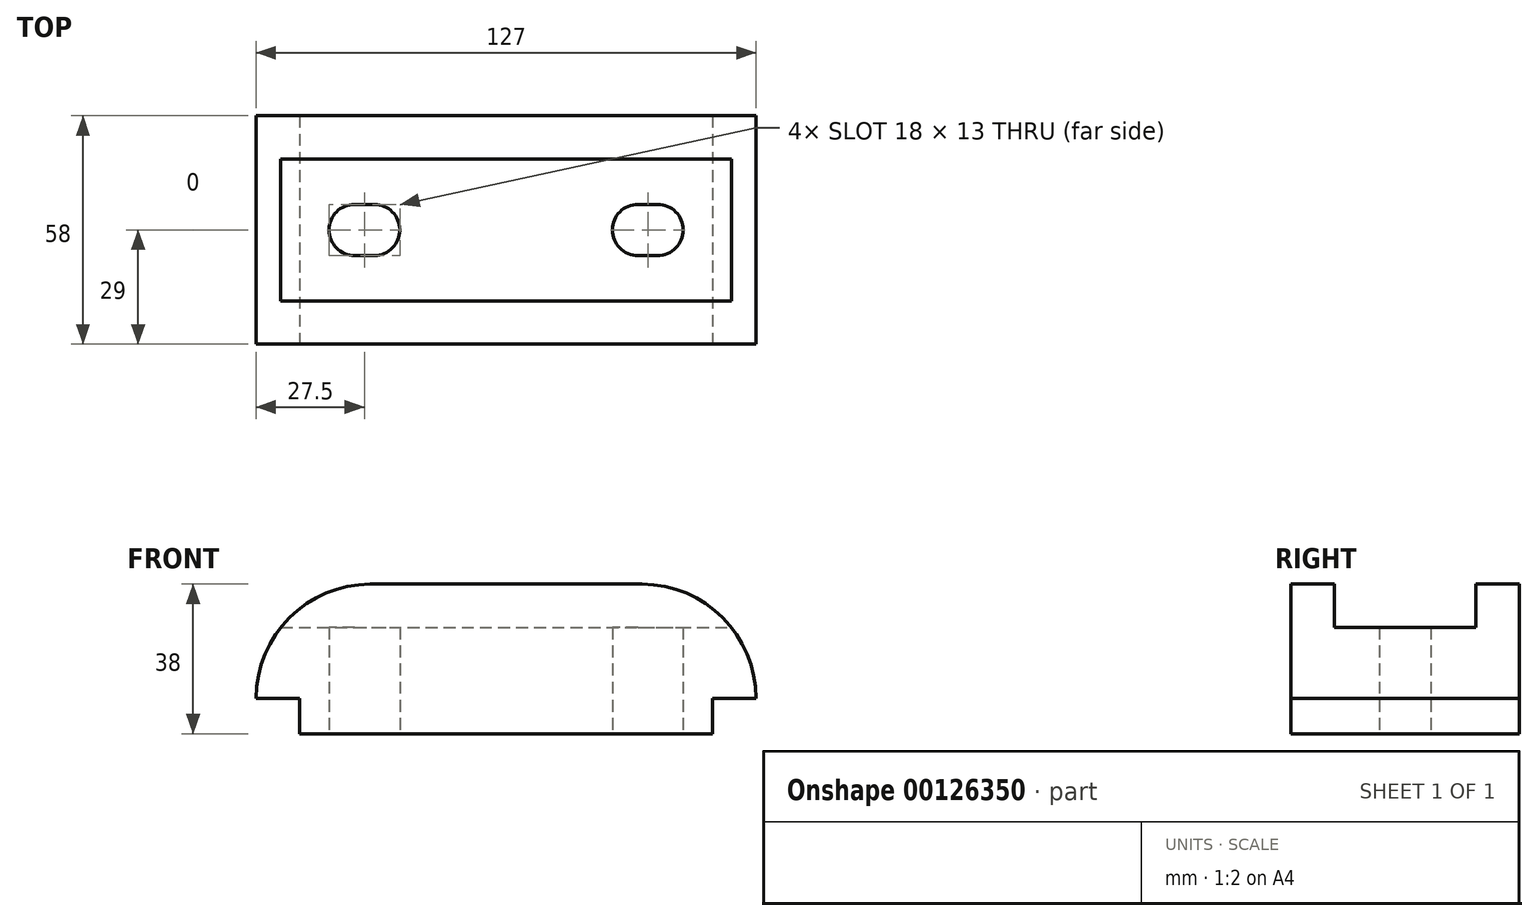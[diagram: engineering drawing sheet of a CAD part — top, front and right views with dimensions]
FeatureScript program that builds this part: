
annotation { "Feature Type Name" : "Feature", "Feature Type Description" : "" }
export const myFeature = defineFeature(function(context is Context, id is Id, definition is map)
    precondition{}
    {
        {
            var Q0;
            Q0=qCreatedBy(makeId("Front.planeOp"),FACE);
            var sketch = newSketch(context, id + "F0", { "sketchPlane" : qUnion([Q0])});
            skLineSegment(sketch, "E0", {"start": v(-63.5, 0) * mm, "end": v(63.5, 0) * mm});
            skLineSegment(sketch, "E1", {"start": v(52.5, 0) * mm, "end": v(52.5, 9) * mm});
            skLineSegment(sketch, "E2", {"start": v(52.5, 9) * mm, "end": v(63.5, 9) * mm});
            skLineSegment(sketch, "E3", {"start": v(-52.5, 0) * mm, "end": v(-52.5, 9) * mm});
            skLineSegment(sketch, "E4", {"start": v(-52.5, 9) * mm, "end": v(-63.5, 9) * mm});
            skLineSegment(sketch, "E5", {"start": v(63.5, 0) * mm, "end": v(63.5, 9) * mm, "construction": true});
            skLineSegment(sketch, "E6", {"start": v(-63.5, 0) * mm, "end": v(-63.5, 9) * mm, "construction": true});
            skPoint(sketch, "E7", {"position": v(0, 38) * mm});
            skLineSegment(sketch, "E8", {"start": v(-34.5, 38) * mm, "end": v(34.5, 38) * mm});
            skLineSegment(sketch, "E9", {"start": v(63.5, 9) * mm, "end": v(63.5, 9) * mm});
            skLineSegment(sketch, "E10", {"start": v(-63.5, 9) * mm, "end": v(-63.5, 9) * mm});
            skPoint(sketch, "E11.visualSharp", {"position": v(-63.5, 38) * mm});
            skArc(sketch, "E11.filletArc", {"start": v(-34.5, 38) * mm, "mid": v(-55, 29.5) * mm, "end": v(-63.5, 9) * mm});
            skPoint(sketch, "E12.visualSharp", {"position": v(63.5, 38) * mm});
            skArc(sketch, "E12.filletArc", {"start": v(63.5, 9) * mm, "mid": v(55, 29.5) * mm, "end": v(34.5, 38) * mm});
            skSolve(sketch);
        }
        {
            var Q0;
            Q0 = qSketchRegion(id + "F0", true);
            extrude(context, id + "F1", {"entities" : qUnion([Q0]), "oppositeDirection" : true, "depth" : 58 * mm});
        }
        {
            var Q0;
            Q0=qCreatedBy(makeId("Right.planeOp"),FACE);
            var sketch = newSketch(context, id + "F2", { "sketchPlane" : qUnion([Q0])});
            skPoint(sketch, "E13", {"position": v(47, 38) * mm});
            skPoint(sketch, "E14", {"position": v(11, 38) * mm});
            skLineSegment(sketch, "E15.bottom", {"start": v(11, 38) * mm, "end": v(47, 38) * mm});
            skLineSegment(sketch, "E15.top", {"start": v(11, 27) * mm, "end": v(47, 27) * mm});
            skLineSegment(sketch, "E15.left", {"start": v(11, 38) * mm, "end": v(11, 27) * mm});
            skLineSegment(sketch, "E15.right", {"start": v(47, 38) * mm, "end": v(47, 27) * mm});
            skSolve(sketch);
        }
        {
            var Q0;
            Q0 = qSketchRegion(id + "F2", true);
            extrude(context, id + "F3", {"entities" : qUnion([Q0]), "operationType" : NewBodyOperationType.REMOVE, "endBound" : BoundingType.THROUGH_ALL, "oppositeDirection" : true, "depth" : 25 * mm, "hasSecondDirection" : true, "secondDirectionBound" : SecondDirectionBoundingType.THROUGH_ALL, "secondDirectionOppositeDirection" : false, "secondDirectionDepth" : 25 * mm});
        }
        {
            var Q0;
            Q0=qCreatedBy(makeId("Top.planeOp"),FACE);
            var sketch = newSketch(context, id + "F4", { "sketchPlane" : qUnion([Q0])});
            skLineSegment(sketch, "E16", {"start": v(-38.5, 35.5) * mm, "end": v(-33.5, 35.5) * mm});
            skLineSegment(sketch, "E17", {"start": v(-38.5, 22.5) * mm, "end": v(-33.5, 22.5) * mm});
            skArc(sketch, "E18", {"start": v(-33.5, 22.5) * mm, "mid": v(-27, 29) * mm, "end": v(-33.5, 35.5) * mm});
            skArc(sketch, "E19", {"start": v(-38.5, 35.5) * mm, "mid": v(-45, 29) * mm, "end": v(-38.5, 22.5) * mm});
            skLineSegment(sketch, "E20.0", {"start": v(-34.5, 0) * mm, "end": v(-63.5, 0) * mm, "construction": true});
            skLineSegment(sketch, "E21.0", {"start": v(-34.5, 0) * mm, "end": v(34.5, 0) * mm, "construction": true});
            skLineSegment(sketch, "E22.0", {"start": v(63.5, 0) * mm, "end": v(34.5, 0) * mm, "construction": true});
            skLineSegment(sketch, "E23.0", {"start": v(-63.5, 58) * mm, "end": v(-63.5, 0) * mm, "construction": true});
            skLineSegment(sketch, "E24", {"start": v(-63.5, 29) * mm, "end": v(63.5, 29) * mm, "construction": true});
            skLineSegment(sketch, "E25.0", {"start": v(63.5, 58) * mm, "end": v(63.5, 0) * mm, "construction": true});
            skLineSegment(sketch, "E26", {"start": v(33.5, 35.5) * mm, "end": v(38.5, 35.5) * mm});
            skLineSegment(sketch, "E27", {"start": v(33.5, 22.5) * mm, "end": v(38.5, 22.5) * mm});
            skArc(sketch, "E28", {"start": v(38.5, 22.5) * mm, "mid": v(45, 29) * mm, "end": v(38.5, 35.5) * mm});
            skArc(sketch, "E29", {"start": v(33.5, 35.5) * mm, "mid": v(27, 29) * mm, "end": v(33.5, 22.5) * mm});
            skSolve(sketch);
        }
        {
            var Q0;
            Q0 = qSketchRegion(id + "F4", true);
            extrude(context, id + "F5", {"entities" : qUnion([Q0]), "operationType" : NewBodyOperationType.REMOVE, "endBound" : BoundingType.THROUGH_ALL, "depth" : 25 * mm});
        }
    });
